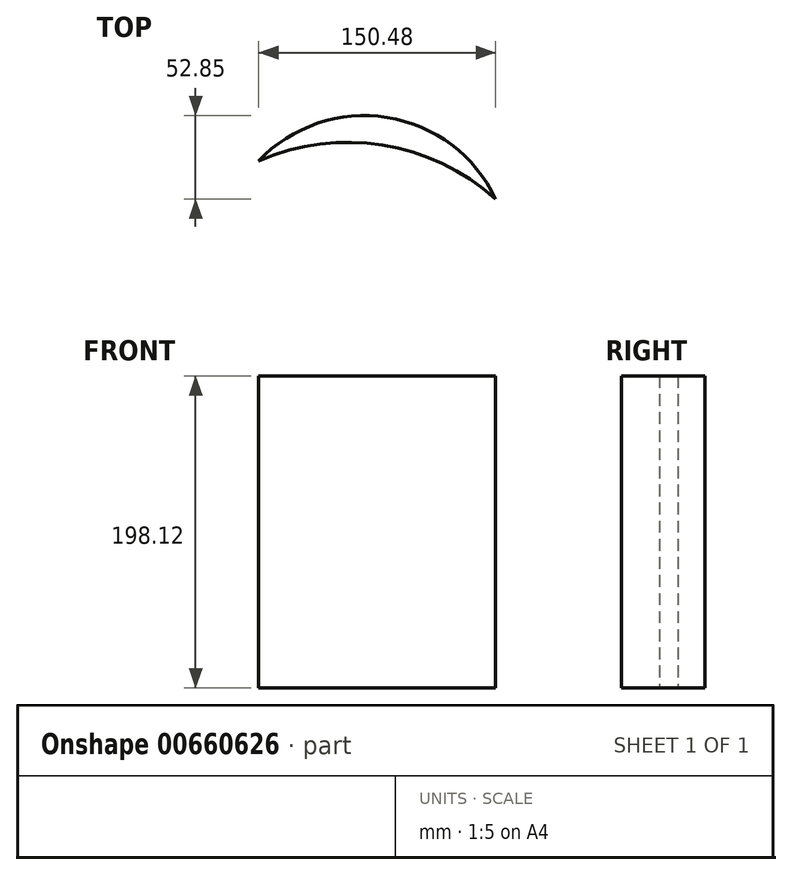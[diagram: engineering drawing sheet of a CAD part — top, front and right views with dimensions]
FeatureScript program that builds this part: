
annotation { "Feature Type Name" : "Feature", "Feature Type Description" : "" }
export const myFeature = defineFeature(function(context is Context, id is Id, definition is map)
    precondition{}
    {
        {
            var Q0;
            Q0=qCreatedBy(makeId("Top.planeOp"),FACE);
            var sketch = newSketch(context, id + "F0", { "sketchPlane" : qUnion([Q0])});
            skArc(sketch, "E0", {"start": v(52.98, -24.09) * mm, "mid": v(-15.91, 27.6) * mm, "end": v(-97.5, 0) * mm});
            skArc(sketch, "E1", {"start": v(52.98, -24.09) * mm, "mid": v(-18.72, 10.04) * mm, "end": v(-97.5, 0) * mm});
            skSolve(sketch);
        }
        {
            var Q0;
            Q0 = qSketchRegion(id + "F0", true);
            extrude(context, id + "F1", {"entities" : qUnion([Q0]), "endBound" : BoundingType.SYMMETRIC, "depth" : 198.12 * mm, "offsetDistance" : 25.4 * mm});
        }
    });
